# Revit family: MOMENTUM_LAYERS_CABANA LAYER_MOD
name_source: partatom
category: Generic Models
units: mm (PartAtom-declared; Revit-internal decimal feet)

## family parameters
Always vertical = Yes
Can host rebar = No
Cut with Voids When Loaded = No
Maintain Annotation Orientation = No
Part Type = Normal
Room Calculation Point = No
Round Connector Dimension = Use Diameter
Shared = No
Work Plane-Based = No

## types (2) — shared parameters
Assembly Code = C3010140
Description = ARCHITECTURAL LAYERS: Light and dark, in wood-inspired print or solid colors, CABANA slats (2.375") add an architectural element to high-sound interiors. Vertical or horizontal create depth and complexity in sleek spaces. Made from recycled PET felt (1" thick), Red List free with an NRC value of 0.45-0.9.
Installation Type = Construction Adhesive
Instruction Sheet Link = https://momentumtextilesandwalls-res.cloudinary.com
Keynote = 09840.A1
Manufacturer = Momentum
Material = 1/2" PET Felt
Pindrop Color = Pindrop - Solid Color - Black
Product Documetation Link = https://momentumtextilesandwalls.com
URL = https://momentumtextilesandwalls.com
Warranty URL = https://momentumtextilesandwalls.com
zero-valued in all types: Cost, Default Elevation

## per-type parameters (varying)
| type | Pindrop Color Top | Product Name |
| Pindrop Layers Cabana - Solid Color | Pindrop - Solid Color - Beige | PINDROP CABANA - Solid Color |
| Pindrop Layers Cabana - Zuri | Pindrop - Zuri Weathered Oak | PINDROP CABANA - Zuri |

## geometry (parser evidence)
native form markers: Sweep x3
no freeform markers — native parametric forms only
